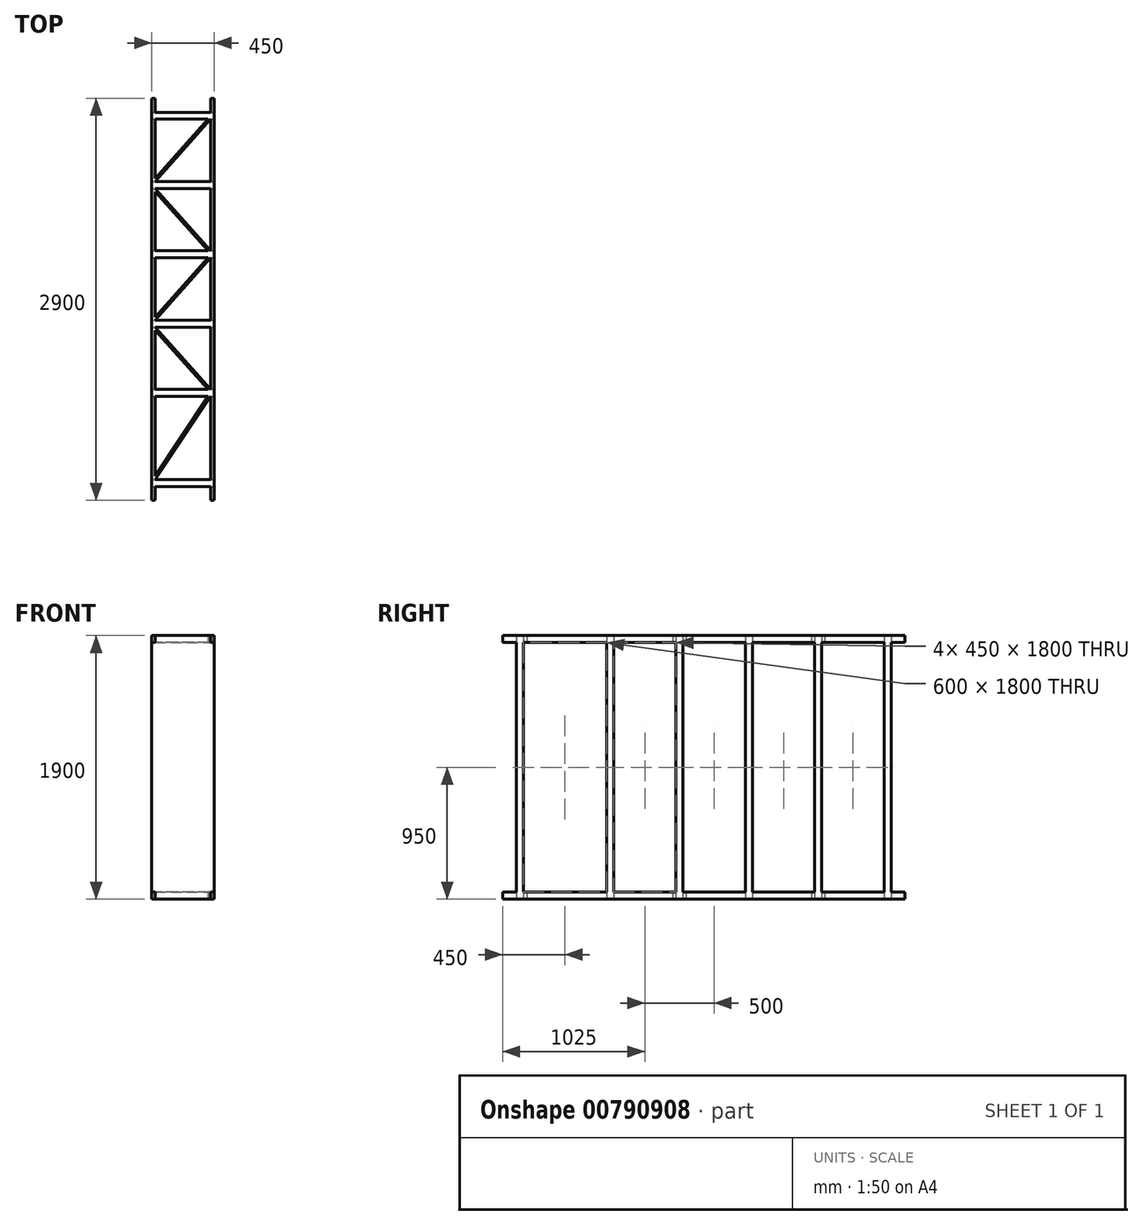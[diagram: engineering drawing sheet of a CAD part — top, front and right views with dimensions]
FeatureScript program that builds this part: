
annotation { "Feature Type Name" : "Feature", "Feature Type Description" : "" }
export const myFeature = defineFeature(function(context is Context, id is Id, definition is map)
    precondition{}
    {
        {
            var Q0;
            Q0=qCreatedBy(makeId("Top.planeOp"),FACE);
            var sketch = newSketch(context, id + "F0", { "sketchPlane" : qUnion([Q0])});
            skLineSegment(sketch, "E0.bottom", {"start": v(0, 0) * mm, "end": v(-450, 0) * mm});
            skLineSegment(sketch, "E0.top", {"start": v(0, 2900) * mm, "end": v(-450, 2900) * mm});
            skLineSegment(sketch, "E0.left", {"start": v(0, 0) * mm, "end": v(0, 2900) * mm});
            skLineSegment(sketch, "E0.right", {"start": v(-450, 0) * mm, "end": v(-450, 2900) * mm});
            skSolve(sketch);
        }
        {
            var Q0;
            Q0 = qSketchRegion(id + "F0", true);
            extrude(context, id + "F1", {"entities" : qUnion([Q0]), "depth" : 1900 * mm, "offsetDistance" : 25 * mm});
        }
        {
            var Q0;
            Q0=makeQuery(id+"F1.opExtrude","SWEPT_FACE",FACE,{"disambiguationData":[OSD([sQuery(id+"F0.wireOp",EDGE,"E0.left")])]});
            var sketch = newSketch(context, id + "F2", { "sketchPlane" : qUnion([Q0])});
            skLineSegment(sketch, "E1.0.0", {"start": v(0, 0) * mm, "end": v(2900, 0) * mm});
            skLineSegment(sketch, "E1.0.1", {"start": v(2900, 0) * mm, "end": v(2900, 1900) * mm});
            skLineSegment(sketch, "E1.0.2", {"start": v(2900, 1900) * mm, "end": v(0, 1900) * mm});
            skLineSegment(sketch, "E1.0.3", {"start": v(0, 1900) * mm, "end": v(0, 0) * mm});
            skLineSegment(sketch, "E2.bottom", {"start": v(2900, 1850) * mm, "end": v(2800, 1850) * mm});
            skLineSegment(sketch, "E2.top", {"start": v(2900, 50) * mm, "end": v(2800, 50) * mm});
            skLineSegment(sketch, "E2.left", {"start": v(2900, 1850) * mm, "end": v(2900, 50) * mm});
            skLineSegment(sketch, "E2.right", {"start": v(2800, 1850) * mm, "end": v(2800, 50) * mm});
            skLineSegment(sketch, "E3.bottom", {"start": v(2750, 1850) * mm, "end": v(2300, 1850) * mm});
            skLineSegment(sketch, "E3.top", {"start": v(2750, 50) * mm, "end": v(2300, 50) * mm});
            skLineSegment(sketch, "E3.left", {"start": v(2750, 1850) * mm, "end": v(2750, 50) * mm});
            skLineSegment(sketch, "E3.right", {"start": v(2300, 1850) * mm, "end": v(2300, 50) * mm});
            skLineSegment(sketch, "E4.bottom", {"start": v(0, 1850) * mm, "end": v(100, 1850) * mm});
            skLineSegment(sketch, "E4.top", {"start": v(0, 50) * mm, "end": v(100, 50) * mm});
            skLineSegment(sketch, "E4.left", {"start": v(0, 1850) * mm, "end": v(0, 50) * mm});
            skLineSegment(sketch, "E4.right", {"start": v(100, 1850) * mm, "end": v(100, 50) * mm});
            skLineSegment(sketch, "E5.bottom", {"start": v(2250, 1850) * mm, "end": v(1800, 1850) * mm});
            skLineSegment(sketch, "E5.top", {"start": v(2250, 50) * mm, "end": v(1800, 50) * mm});
            skLineSegment(sketch, "E5.left", {"start": v(2250, 1850) * mm, "end": v(2250, 50) * mm});
            skLineSegment(sketch, "E5.right", {"start": v(1800, 1850) * mm, "end": v(1800, 50) * mm});
            skLineSegment(sketch, "E6.bottom", {"start": v(150, 1850) * mm, "end": v(750, 1850) * mm});
            skLineSegment(sketch, "E6.top", {"start": v(150, 50) * mm, "end": v(750, 50) * mm});
            skLineSegment(sketch, "E6.left", {"start": v(150, 1850) * mm, "end": v(150, 50) * mm});
            skLineSegment(sketch, "E6.right", {"start": v(750, 1850) * mm, "end": v(750, 50) * mm});
            skLineSegment(sketch, "E7.bottom", {"start": v(1750, 1850) * mm, "end": v(1300, 1850) * mm});
            skLineSegment(sketch, "E7.top", {"start": v(1750, 50) * mm, "end": v(1300, 50) * mm});
            skLineSegment(sketch, "E7.left", {"start": v(1750, 1850) * mm, "end": v(1750, 50) * mm});
            skLineSegment(sketch, "E7.right", {"start": v(1300, 1850) * mm, "end": v(1300, 50) * mm});
            skLineSegment(sketch, "E8.bottom", {"start": v(1250, 1850) * mm, "end": v(800, 1850) * mm});
            skLineSegment(sketch, "E8.top", {"start": v(1250, 50) * mm, "end": v(800, 50) * mm});
            skLineSegment(sketch, "E8.left", {"start": v(1250, 1850) * mm, "end": v(1250, 50) * mm});
            skLineSegment(sketch, "E8.right", {"start": v(800, 1850) * mm, "end": v(800, 50) * mm});
            skSolve(sketch);
        }
        {
            var Q0;
            Q0=makeQuery(id+"F2.imprint","IMPRINT",FACE,{"disambiguationData":[TD([[makeQuery(id+"F2.imprint","IMPRINT",EDGE,{"derivedFrom":sQuery(id+"F2.wireOp",EDGE,"E4.bottom")}),-1.0]])]});
            var Q1;
            Q1=makeQuery(id+"F2.imprint","IMPRINT",FACE,{"disambiguationData":[TD([[makeQuery(id+"F2.imprint","IMPRINT",EDGE,{"derivedFrom":sQuery(id+"F2.wireOp",EDGE,"E6.bottom")}),-1.0]])]});
            var Q2;
            Q2=makeQuery(id+"F2.imprint","IMPRINT",FACE,{"disambiguationData":[TD([[makeQuery(id+"F2.imprint","IMPRINT",EDGE,{"derivedFrom":sQuery(id+"F2.wireOp",EDGE,"E8.bottom")}),1.0]])]});
            var Q3;
            Q3=makeQuery(id+"F2.imprint","IMPRINT",FACE,{"disambiguationData":[TD([[makeQuery(id+"F2.imprint","IMPRINT",EDGE,{"derivedFrom":sQuery(id+"F2.wireOp",EDGE,"E7.bottom")}),1.0]])]});
            var Q4;
            Q4=makeQuery(id+"F2.imprint","IMPRINT",FACE,{"disambiguationData":[TD([[makeQuery(id+"F2.imprint","IMPRINT",EDGE,{"derivedFrom":sQuery(id+"F2.wireOp",EDGE,"E5.bottom")}),1.0]])]});
            var Q5;
            Q5=makeQuery(id+"F2.imprint","IMPRINT",FACE,{"disambiguationData":[TD([[makeQuery(id+"F2.imprint","IMPRINT",EDGE,{"derivedFrom":sQuery(id+"F2.wireOp",EDGE,"E3.bottom")}),1.0]])]});
            var Q6;
            Q6=makeQuery(id+"F2.imprint","IMPRINT",FACE,{"disambiguationData":[TD([[makeQuery(id+"F2.imprint","IMPRINT",EDGE,{"derivedFrom":sQuery(id+"F2.wireOp",EDGE,"E2.bottom")}),1.0]])]});
            extrude(context, id + "F3", {"entities" : qUnion([Q0, Q1, Q2, Q3, Q4, Q5, Q6]), "operationType" : NewBodyOperationType.REMOVE, "oppositeDirection" : true, "depth" : 450 * mm, "offsetDistance" : 25 * mm});
        }
        {
            var Q0;
            Q0=makeQuery(id+"F1.opExtrude","CAP_FACE",FACE,{"disambiguationData":[OSD([sQuery(id+"F0.wireOp",EDGE,"E0.bottom"),sQuery(id+"F0.wireOp",EDGE,"E0.top"),sQuery(id+"F0.wireOp",EDGE,"E0.left"),sQuery(id+"F0.wireOp",EDGE,"E0.right")])],"isStart":true});
            var sketch = newSketch(context, id + "F4", { "sketchPlane" : qUnion([Q0])});
            skLineSegment(sketch, "E9.bottom", {"start": v(-425, 0) * mm, "end": v(-25, 0) * mm});
            skLineSegment(sketch, "E9.top", {"start": v(-425, -100) * mm, "end": v(-25, -100) * mm});
            skLineSegment(sketch, "E9.left", {"start": v(-425, 0) * mm, "end": v(-425, -100) * mm});
            skLineSegment(sketch, "E9.right", {"start": v(-25, 0) * mm, "end": v(-25, -100) * mm});
            skLineSegment(sketch, "E10.bottom", {"start": v(-425, -150) * mm, "end": v(-25, -150) * mm});
            skLineSegment(sketch, "E10.top", {"start": v(-425, -750) * mm, "end": v(-43.03, -750) * mm});
            skLineSegment(sketch, "E10.left", {"start": v(-425, -177.04) * mm, "end": v(-425, -750) * mm});
            skLineSegment(sketch, "E10.right", {"start": v(-25, -150) * mm, "end": v(-25, -750) * mm});
            skLineSegment(sketch, "E11.bottom", {"start": v(-425, -800) * mm, "end": v(-45.07, -800) * mm});
            skLineSegment(sketch, "E11.top", {"start": v(-425, -1250) * mm, "end": v(-25, -1250) * mm});
            skLineSegment(sketch, "E11.left", {"start": v(-425, -800) * mm, "end": v(-425, -1227.42) * mm});
            skLineSegment(sketch, "E11.right", {"start": v(-25, -800) * mm, "end": v(-25, -1250) * mm});
            skLineSegment(sketch, "E12.bottom", {"start": v(-425, -1300) * mm, "end": v(-25, -1300) * mm});
            skLineSegment(sketch, "E12.top", {"start": v(-425, -1750) * mm, "end": v(-45.07, -1750) * mm});
            skLineSegment(sketch, "E12.left", {"start": v(-425, -1322.58) * mm, "end": v(-425, -1750) * mm});
            skLineSegment(sketch, "E12.right", {"start": v(-25, -1300) * mm, "end": v(-25, -1750) * mm});
            skLineSegment(sketch, "E13.bottom", {"start": v(-425, -1800) * mm, "end": v(-45.07, -1800) * mm});
            skLineSegment(sketch, "E13.top", {"start": v(-425, -2250) * mm, "end": v(-25, -2250) * mm});
            skLineSegment(sketch, "E13.left", {"start": v(-425, -1800) * mm, "end": v(-425, -2227.42) * mm});
            skLineSegment(sketch, "E13.right", {"start": v(-25, -1800) * mm, "end": v(-25, -2250) * mm});
            skLineSegment(sketch, "E14.bottom", {"start": v(-425, -2300) * mm, "end": v(-25, -2300) * mm});
            skLineSegment(sketch, "E14.top", {"start": v(-425, -2750) * mm, "end": v(-45.07, -2750) * mm});
            skLineSegment(sketch, "E14.left", {"start": v(-425, -2322.58) * mm, "end": v(-425, -2750) * mm});
            skLineSegment(sketch, "E14.right", {"start": v(-25, -2300) * mm, "end": v(-25, -2750) * mm});
            skLineSegment(sketch, "E15.bottom", {"start": v(-425, -2900) * mm, "end": v(-25, -2900) * mm});
            skLineSegment(sketch, "E15.top", {"start": v(-425, -2800) * mm, "end": v(-25, -2800) * mm});
            skLineSegment(sketch, "E15.left", {"start": v(-425, -2900) * mm, "end": v(-425, -2800) * mm});
            skLineSegment(sketch, "E15.right", {"start": v(-25, -2900) * mm, "end": v(-25, -2800) * mm});
            skLineSegment(sketch, "E16", {"start": v(-425, -150) * mm, "end": v(-25, -750) * mm});
            skLineSegment(sketch, "E17", {"start": v(-25, -800) * mm, "end": v(-425, -1250) * mm});
            skLineSegment(sketch, "E18", {"start": v(-425, -1300) * mm, "end": v(-25, -1750) * mm});
            skLineSegment(sketch, "E19", {"start": v(-25, -1800) * mm, "end": v(-425, -2250) * mm});
            skLineSegment(sketch, "E20", {"start": v(-425, -2300) * mm, "end": v(-25, -2750) * mm});
            skLineSegment(sketch, "E21", {"start": v(-45.07, -2750) * mm, "end": v(-425, -2322.58) * mm});
            skLineSegment(sketch, "E22", {"start": v(-425, -2227.42) * mm, "end": v(-45.07, -1800) * mm});
            skLineSegment(sketch, "E23", {"start": v(-45.07, -1750) * mm, "end": v(-425, -1322.58) * mm});
            skLineSegment(sketch, "E24", {"start": v(-425, -1227.42) * mm, "end": v(-45.07, -800) * mm});
            skLineSegment(sketch, "E25", {"start": v(-43.03, -750) * mm, "end": v(-425, -177.04) * mm});
            skSolve(sketch);
        }
        {
            var Q0;
            Q0=makeQuery(id+"F4.imprint","IMPRINT",FACE,{"disambiguationData":[TD([[makeQuery(id+"F4.imprint","IMPRINT",EDGE,{"derivedFrom":sQuery(id+"F4.wireOp",EDGE,"E9.bottom")}),1.0]])]});
            var Q1;
            Q1=makeQuery(id+"F4.imprint","IMPRINT",FACE,{"disambiguationData":[TD([[makeQuery(id+"F4.imprint","IMPRINT",EDGE,{"derivedFrom":sQuery(id+"F4.wireOp",EDGE,"E10.bottom")}),-1.0]])]});
            var Q2;
            Q2=makeQuery(id+"F4.imprint","IMPRINT",FACE,{"disambiguationData":[TD([[makeQuery(id+"F4.imprint","IMPRINT",EDGE,{"derivedFrom":sQuery(id+"F4.wireOp",EDGE,"E10.top")}),1.0]])]});
            var Q3;
            Q3=makeQuery(id+"F4.imprint","IMPRINT",FACE,{"disambiguationData":[TD([[makeQuery(id+"F4.imprint","IMPRINT",EDGE,{"derivedFrom":sQuery(id+"F4.wireOp",EDGE,"E11.bottom")}),-1.0]])]});
            var Q4;
            Q4=makeQuery(id+"F4.imprint","IMPRINT",FACE,{"disambiguationData":[TD([[makeQuery(id+"F4.imprint","IMPRINT",EDGE,{"derivedFrom":sQuery(id+"F4.wireOp",EDGE,"E11.top")}),1.0]])]});
            var Q5;
            Q5=makeQuery(id+"F4.imprint","IMPRINT",FACE,{"disambiguationData":[TD([[makeQuery(id+"F4.imprint","IMPRINT",EDGE,{"derivedFrom":sQuery(id+"F4.wireOp",EDGE,"E12.bottom")}),-1.0]])]});
            var Q6;
            Q6=makeQuery(id+"F4.imprint","IMPRINT",FACE,{"disambiguationData":[TD([[makeQuery(id+"F4.imprint","IMPRINT",EDGE,{"derivedFrom":sQuery(id+"F4.wireOp",EDGE,"E12.top")}),1.0]])]});
            var Q7;
            Q7=makeQuery(id+"F4.imprint","IMPRINT",FACE,{"disambiguationData":[TD([[makeQuery(id+"F4.imprint","IMPRINT",EDGE,{"derivedFrom":sQuery(id+"F4.wireOp",EDGE,"E13.bottom")}),-1.0]])]});
            var Q8;
            Q8=makeQuery(id+"F4.imprint","IMPRINT",FACE,{"disambiguationData":[TD([[makeQuery(id+"F4.imprint","IMPRINT",EDGE,{"derivedFrom":sQuery(id+"F4.wireOp",EDGE,"E13.top")}),1.0]])]});
            var Q9;
            Q9=makeQuery(id+"F4.imprint","IMPRINT",FACE,{"disambiguationData":[TD([[makeQuery(id+"F4.imprint","IMPRINT",EDGE,{"derivedFrom":sQuery(id+"F4.wireOp",EDGE,"E14.top")}),1.0]])]});
            var Q10;
            Q10=makeQuery(id+"F4.imprint","IMPRINT",FACE,{"disambiguationData":[TD([[makeQuery(id+"F4.imprint","IMPRINT",EDGE,{"derivedFrom":sQuery(id+"F4.wireOp",EDGE,"E14.bottom")}),-1.0]])]});
            var Q11;
            Q11=makeQuery(id+"F4.imprint","IMPRINT",FACE,{"disambiguationData":[TD([[makeQuery(id+"F4.imprint","IMPRINT",EDGE,{"derivedFrom":sQuery(id+"F4.wireOp",EDGE,"E15.bottom")}),-1.0]])]});
            extrude(context, id + "F5", {"entities" : qUnion([Q0, Q1, Q2, Q3, Q4, Q5, Q6, Q7, Q8, Q9, Q10, Q11]), "operationType" : NewBodyOperationType.REMOVE, "oppositeDirection" : true, "depth" : 2900 * mm, "offsetDistance" : 25 * mm});
        }
    });
